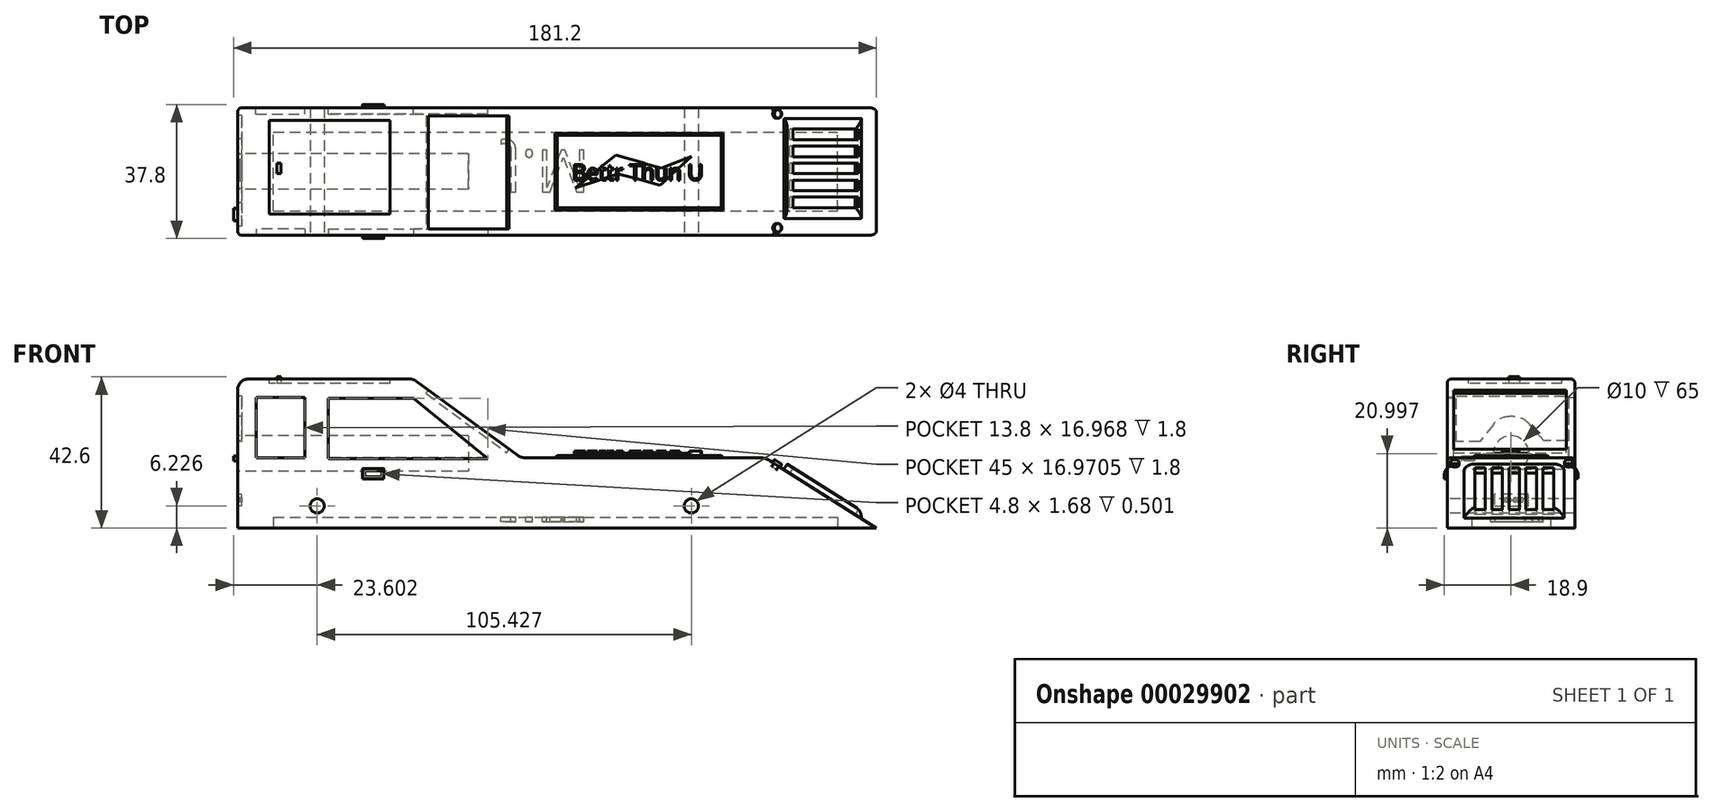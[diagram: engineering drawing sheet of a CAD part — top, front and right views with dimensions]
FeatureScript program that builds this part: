
annotation { "Feature Type Name" : "Feature", "Feature Type Description" : "" }
export const myFeature = defineFeature(function(context is Context, id is Id, definition is map)
    precondition{}
    {
        {
            var Q0;
            Q0=qCreatedBy(makeId("Front.planeOp"),FACE);
            var sketch = newSketch(context, id + "F0", { "sketchPlane" : qUnion([Q0])});
            skLineSegment(sketch, "E0.bottom", {"start": v(-82.47, -33.07) * mm, "end": v(217.53, -33.07) * mm});
            skLineSegment(sketch, "E0.left", {"start": v(-82.47, -33.07) * mm, "end": v(-82.47, 36.93) * mm});
            skLineSegment(sketch, "E1", {"start": v(217.53, -33.07) * mm, "end": v(165.18, 0) * mm});
            skLineSegment(sketch, "E2", {"start": v(165.18, 0) * mm, "end": v(50.43, 0) * mm});
            skLineSegment(sketch, "E3", {"start": v(50.43, 0) * mm, "end": v(0, 36.93) * mm});
            skLineSegment(sketch, "E4", {"start": v(0, 36.93) * mm, "end": v(-82.47, 36.93) * mm});
            skSolve(sketch);
        }
        {
            var Q0;
            Q0=makeQuery(id+"F0.imprint","IMPRINT",FACE,{"disambiguationData":[TD([[makeQuery(id+"F0.imprint","IMPRINT",EDGE,{"derivedFrom":sQuery(id+"F0.wireOp",EDGE,"E0.bottom")}),1.0]])]});
            extrude(context, id + "F1", {"entities" : qUnion([Q0]), "depth" : 60 * mm});
        }
        {
            var Q0;
            Q0=makeQuery(id+"F1.opExtrude","SWEPT_FACE",FACE,{"disambiguationData":[OSD([sQuery(id+"F0.wireOp",EDGE,"E0.left")])]});
            var sketch = newSketch(context, id + "F2", { "sketchPlane" : qUnion([Q0])});
            skCircle(sketch, "E5", {"center": v(30, 1.93) * mm, "radius": 5 * mm});
            skSolve(sketch);
        }
        {
            var Q0;
            Q0=makeQuery(id+"F2.imprint","IMPRINT",FACE,{"disambiguationData":[TD([[makeQuery(id+"F2.imprint","IMPRINT",EDGE,{"derivedFrom":sQuery(id+"F2.wireOp",EDGE,"E5")}),1.0]])]});
            extrude(context, id + "F3", {"entities" : qUnion([Q0]), "operationType" : NewBodyOperationType.REMOVE, "oppositeDirection" : true, "depth" : 65 * mm});
        }
        {
            var Q0;
            Q0=makeQuery(id+"F1.opExtrude","SWEPT_EDGE",EDGE,{"disambiguationData":[OSD([sQuery(id+"F0.wireOp",EDGE,"E1"),sQuery(id+"F0.wireOp",EDGE,"E2")])]});
            fillet(context, id + "F4", {"entities" : qUnion([Q0]), "radius" : 10 * mm, "tangentPropagation" : true, "allowEdgeOverflow" : false});
        }
        {
            var Q0;
            Q0=makeQuery(id+"F1.opExtrude","SWEPT_EDGE",EDGE,{"disambiguationData":[OSD([sQuery(id+"F0.wireOp",EDGE,"E2"),sQuery(id+"F0.wireOp",EDGE,"E3")])]});
            var Q1;
            Q1=makeQuery(id+"F1.opExtrude","SWEPT_EDGE",EDGE,{"disambiguationData":[OSD([sQuery(id+"F0.wireOp",EDGE,"E3"),sQuery(id+"F0.wireOp",EDGE,"E4")])]});
            fillet(context, id + "F5", {"entities" : qUnion([Q0, Q1]), "radius" : 5 * mm, "tangentPropagation" : true, "allowEdgeOverflow" : false});
        }
        {
            var Q0;
            Q0=makeQuery(id+"F1.opExtrude","CAP_FACE",FACE,{"disambiguationData":[OSD([sQuery(id+"F0.wireOp",EDGE,"E0.bottom"),sQuery(id+"F0.wireOp",EDGE,"E0.left"),sQuery(id+"F0.wireOp",EDGE,"E1"),sQuery(id+"F0.wireOp",EDGE,"E2"),sQuery(id+"F0.wireOp",EDGE,"E3"),sQuery(id+"F0.wireOp",EDGE,"E4")])],"isStart":false});
            var sketch = newSketch(context, id + "F6", { "sketchPlane" : qUnion([Q0])});
            skLineSegment(sketch, "E6", {"start": v(0, 27.87) * mm, "end": v(0, 27.87) * mm});
            skLineSegment(sketch, "E7", {"start": v(-40, -0.41) * mm, "end": v(-40, 27.87) * mm});
            skLineSegment(sketch, "E8", {"start": v(-40, 27.87) * mm, "end": v(0, 27.87) * mm});
            skLineSegment(sketch, "E9", {"start": v(-40, -0.41) * mm, "end": v(35, -0.41) * mm});
            skLineSegment(sketch, "E10", {"start": v(35, -0.41) * mm, "end": v(0, 27.87) * mm});
            skLineSegment(sketch, "E11", {"start": v(-73.89, 28.28) * mm, "end": v(-73.89, 0) * mm});
            skLineSegment(sketch, "E12", {"start": v(-50.89, 0) * mm, "end": v(-50.89, 28.28) * mm});
            skLineSegment(sketch, "E13", {"start": v(-50.89, 28.28) * mm, "end": v(-73.89, 28.28) * mm});
            skLineSegment(sketch, "E14", {"start": v(-73.89, 0) * mm, "end": v(-50.89, 0) * mm});
            skSolve(sketch);
        }
        {
            var Q0;
            Q0=qSketchRegion(id+"F6",true);
            extrude(context, id + "F7", {"entities" : qUnion([Q0]), "operationType" : NewBodyOperationType.REMOVE, "oppositeDirection" : true, "depth" : 3 * mm});
        }
        {
            var Q0;
            Q0=makeQuery(id+"F1.opExtrude","CAP_FACE",FACE,{"disambiguationData":[OSD([sQuery(id+"F0.wireOp",EDGE,"E0.bottom"),sQuery(id+"F0.wireOp",EDGE,"E0.left"),sQuery(id+"F0.wireOp",EDGE,"E1"),sQuery(id+"F0.wireOp",EDGE,"E2"),sQuery(id+"F0.wireOp",EDGE,"E3"),sQuery(id+"F0.wireOp",EDGE,"E4")])],"isStart":true});
            var sketch = newSketch(context, id + "F8", { "sketchPlane" : qUnion([Q0])});
            skLineSegment(sketch, "E15", {"start": v(0, 28.28) * mm, "end": v(-35, 0) * mm});
            skLineSegment(sketch, "E16", {"start": v(-35, 0) * mm, "end": v(40, 0) * mm});
            skLineSegment(sketch, "E17", {"start": v(40, 0) * mm, "end": v(40, 28.28) * mm});
            skLineSegment(sketch, "E18", {"start": v(40, 28.28) * mm, "end": v(0, 28.28) * mm});
            skLineSegment(sketch, "E19", {"start": v(51, 28.28) * mm, "end": v(51, 0) * mm});
            skLineSegment(sketch, "E20", {"start": v(51, 0) * mm, "end": v(74, 0) * mm});
            skLineSegment(sketch, "E21", {"start": v(74, 0) * mm, "end": v(74, 28.28) * mm});
            skLineSegment(sketch, "E22", {"start": v(74, 28.28) * mm, "end": v(51, 28.28) * mm});
            skSolve(sketch);
        }
        {
            var Q0;
            Q0=qSketchRegion(id+"F8",true);
            extrude(context, id + "F9", {"entities" : qUnion([Q0]), "operationType" : NewBodyOperationType.REMOVE, "oppositeDirection" : true, "depth" : 3 * mm});
        }
        {
            var Q0;
            Q0=makeQuery(id+"F1.opExtrude","SWEPT_FACE",FACE,{"disambiguationData":[OSD([sQuery(id+"F0.wireOp",EDGE,"E3")])]});
            var sketch = newSketch(context, id + "F10", { "sketchPlane" : qUnion([Q0])});
            skLineSegment(sketch, "E23", {"start": v(-13, -56.94) * mm, "end": v(34, -56.94) * mm});
            skLineSegment(sketch, "E24", {"start": v(34, -56.94) * mm, "end": v(34, -3.94) * mm});
            skLineSegment(sketch, "E25", {"start": v(34, -3.94) * mm, "end": v(-13, -3.94) * mm});
            skLineSegment(sketch, "E26", {"start": v(-13, -3.94) * mm, "end": v(-13, -56.94) * mm});
            skSolve(sketch);
        }
        {
            var Q0;
            Q0=qSketchRegion(id+"F10",true);
            extrude(context, id + "F11", {"entities" : qUnion([Q0]), "operationType" : NewBodyOperationType.REMOVE, "oppositeDirection" : true, "depth" : 2 * mm});
        }
        {
            var Q0;
            Q0=makeQuery(id+"F1.opExtrude","SWEPT_EDGE",EDGE,{"disambiguationData":[OSD([sQuery(id+"F0.wireOp",EDGE,"E0.left"),sQuery(id+"F0.wireOp",EDGE,"E4")])]});
            fillet(context, id + "F12", {"entities" : qUnion([Q0]), "radius" : 5 * mm, "tangentPropagation" : true, "allowEdgeOverflow" : false});
        }
        {
            var Q0;
            Q0=makeQuery(id+"F1.opExtrude","CAP_FACE",FACE,{"disambiguationData":[OSD([sQuery(id+"F0.wireOp",EDGE,"E0.bottom"),sQuery(id+"F0.wireOp",EDGE,"E0.left"),sQuery(id+"F0.wireOp",EDGE,"E1"),sQuery(id+"F0.wireOp",EDGE,"E2"),sQuery(id+"F0.wireOp",EDGE,"E3"),sQuery(id+"F0.wireOp",EDGE,"E4")])],"isStart":false});
            var sketch = newSketch(context, id + "F13", { "sketchPlane" : qUnion([Q0])});
            skLineSegment(sketch, "E27", {"start": v(-23.82, -5.07) * mm, "end": v(-13.82, -5.07) * mm});
            skLineSegment(sketch, "E28", {"start": v(-13.82, -5.07) * mm, "end": v(-13.82, -10.07) * mm});
            skLineSegment(sketch, "E29", {"start": v(-13.82, -10.07) * mm, "end": v(-23.82, -10.07) * mm});
            skLineSegment(sketch, "E30", {"start": v(-23.82, -10.07) * mm, "end": v(-23.82, -5.07) * mm});
            skLineSegment(sketch, "E31", {"start": v(-22.8, -6.15) * mm, "end": v(-22.8, -8.95) * mm});
            skLineSegment(sketch, "E32", {"start": v(-22.8, -8.95) * mm, "end": v(-14.8, -8.95) * mm});
            skLineSegment(sketch, "E33", {"start": v(-14.8, -8.95) * mm, "end": v(-14.8, -6.15) * mm});
            skLineSegment(sketch, "E34", {"start": v(-14.8, -6.15) * mm, "end": v(-22.8, -6.15) * mm});
            skSolve(sketch);
        }
        {
            var Q0;
            Q0=qSketchRegion(id+"F13",true);
            extrude(context, id + "F14", {"entities" : qUnion([Q0]), "operationType" : NewBodyOperationType.ADD, "depth" : 1.5 * mm});
        }
        {
            var Q0;
            Q0=makeQuery(id+"F1.opExtrude","CAP_FACE",FACE,{"disambiguationData":[OSD([sQuery(id+"F0.wireOp",EDGE,"E0.bottom"),sQuery(id+"F0.wireOp",EDGE,"E0.left"),sQuery(id+"F0.wireOp",EDGE,"E1"),sQuery(id+"F0.wireOp",EDGE,"E2"),sQuery(id+"F0.wireOp",EDGE,"E3"),sQuery(id+"F0.wireOp",EDGE,"E4")])],"isStart":true});
            var sketch = newSketch(context, id + "F15", { "sketchPlane" : qUnion([Q0])});
            skLineSegment(sketch, "E35", {"start": v(13.79, -4.77) * mm, "end": v(13.79, -9.77) * mm});
            skLineSegment(sketch, "E36", {"start": v(13.79, -9.77) * mm, "end": v(23.79, -9.77) * mm});
            skLineSegment(sketch, "E37", {"start": v(23.79, -9.77) * mm, "end": v(23.79, -4.77) * mm});
            skLineSegment(sketch, "E38", {"start": v(23.79, -4.77) * mm, "end": v(13.79, -4.77) * mm});
            skLineSegment(sketch, "E39", {"start": v(14.77, -5.87) * mm, "end": v(14.77, -8.67) * mm});
            skLineSegment(sketch, "E40", {"start": v(14.77, -8.67) * mm, "end": v(22.77, -8.67) * mm});
            skLineSegment(sketch, "E41", {"start": v(22.77, -8.67) * mm, "end": v(22.77, -5.87) * mm});
            skLineSegment(sketch, "E42", {"start": v(22.77, -5.87) * mm, "end": v(14.77, -5.87) * mm});
            skSolve(sketch);
        }
        {
            var Q0;
            Q0=qSketchRegion(id+"F15",true);
            extrude(context, id + "F16", {"entities" : qUnion([Q0]), "operationType" : NewBodyOperationType.ADD, "depth" : 1.5 * mm});
        }
        {
            var Q0;
            Q0=makeQuery(id+"F16.opExtrude","CAP_EDGE",EDGE,{"disambiguationData":[OSD([sQuery(id+"F15.wireOp",EDGE,"E38")])],"isStart":false});
            fillet(context, id + "F17", {"entities" : qUnion([Q0]), "radius" : 5 * mm, "tangentPropagation" : true, "allowEdgeOverflow" : false});
        }
        {
            var Q0;
            Q0=makeQuery(id+"F14.opExtrude","CAP_EDGE",EDGE,{"disambiguationData":[OSD([sQuery(id+"F13.wireOp",EDGE,"E27")])],"isStart":false});
            fillet(context, id + "F18", {"entities" : qUnion([Q0]), "radius" : 5 * mm, "tangentPropagation" : true, "allowEdgeOverflow" : false});
        }
        {
            var Q0;
            Q0=makeQuery(id+"F1.opExtrude","SWEPT_FACE",FACE,{"disambiguationData":[OSD([sQuery(id+"F0.wireOp",EDGE,"E0.left")])]});
            var sketch = newSketch(context, id + "F19", { "sketchPlane" : qUnion([Q0])});
            skLineSegment(sketch, "E43", {"start": v(3.67, 28.92) * mm, "end": v(3.67, 7.92) * mm});
            skLineSegment(sketch, "E44", {"start": v(3.67, 7.92) * mm, "end": v(14.67, 7.92) * mm});
            skLineSegment(sketch, "E45", {"start": v(14.67, 7.92) * mm, "end": v(21.44, 15.81) * mm});
            skLineSegment(sketch, "E46", {"start": v(29.03, 19.3) * mm, "end": v(30.56, 19.3) * mm});
            skLineSegment(sketch, "E47", {"start": v(38.43, 15.46) * mm, "end": v(44.67, 7.49) * mm});
            skLineSegment(sketch, "E48", {"start": v(44.67, 7.49) * mm, "end": v(55.67, 7.49) * mm});
            skLineSegment(sketch, "E49", {"start": v(55.67, 7.49) * mm, "end": v(55.67, 28.92) * mm});
            skLineSegment(sketch, "E50", {"start": v(55.67, 28.92) * mm, "end": v(3.67, 28.92) * mm});
            skPoint(sketch, "E51.visualSharp", {"position": v(24.43, 19.3) * mm});
            skArc(sketch, "E51.filletArc", {"start": v(29.03, 19.3) * mm, "mid": v(24.85, 18.4) * mm, "end": v(21.44, 15.81) * mm});
            skPoint(sketch, "E52.visualSharp", {"position": v(35.43, 19.3) * mm});
            skArc(sketch, "E52.filletArc", {"start": v(38.43, 15.46) * mm, "mid": v(34.94, 18.3) * mm, "end": v(30.56, 19.3) * mm});
            skLineSegment(sketch, "E53", {"start": v(16.08, 9.56) * mm, "end": v(15.58, 8.97) * mm});
            skLineSegment(sketch, "E54", {"start": v(21.84, -17.18) * mm, "end": v(37.84, -17.18) * mm});
            skLineSegment(sketch, "E55", {"start": v(37.84, -17.18) * mm, "end": v(37.84, -22.68) * mm});
            skLineSegment(sketch, "E56", {"start": v(37.84, -22.68) * mm, "end": v(21.84, -22.68) * mm});
            skLineSegment(sketch, "E57", {"start": v(21.84, -22.68) * mm, "end": v(21.84, -17.18) * mm});
            skText(sketch, "E58", { "text": "062-002", "fontName": "OpenSans-Regular.ttf"});
            const initialGuessF19  = {"E58": [0.0242, -0.02085, 1, 0, 0.002]};
            skSetInitialGuess(sketch, initialGuessF19);
            skSolve(sketch);
        }
        {
            var Q0;
            Q0=makeQuery(id+"F1.opExtrude","SWEPT_FACE",FACE,{"disambiguationData":[OSD([sQuery(id+"F0.wireOp",EDGE,"E1")])]});
            var sketch = newSketch(context, id + "F20", { "sketchPlane" : qUnion([Q0])});
            skLineSegment(sketch, "E59", {"start": v(150.04, -5.03) * mm, "end": v(150.04, -52.03) * mm});
            skLineSegment(sketch, "E60", {"start": v(150.04, -52.03) * mm, "end": v(193.04, -52.03) * mm});
            skLineSegment(sketch, "E61", {"start": v(193.04, -52.03) * mm, "end": v(193.04, -5.03) * mm});
            skLineSegment(sketch, "E62", {"start": v(193.04, -5.03) * mm, "end": v(150.04, -5.03) * mm});
            skLineSegment(sketch, "E63", {"start": v(153.34, -10.03) * mm, "end": v(189.74, -10.03) * mm});
            skLineSegment(sketch, "E64", {"start": v(189.74, -10.03) * mm, "end": v(189.74, -15.03) * mm});
            skLineSegment(sketch, "E65", {"start": v(189.74, -15.03) * mm, "end": v(153.34, -15.03) * mm});
            skLineSegment(sketch, "E66", {"start": v(153.34, -15.03) * mm, "end": v(153.34, -10.03) * mm});
            skLineSegment(sketch, "E67", {"start": v(153.34, -18.03) * mm, "end": v(189.74, -18.03) * mm});
            skLineSegment(sketch, "E68", {"start": v(189.74, -18.03) * mm, "end": v(189.74, -23.03) * mm});
            skLineSegment(sketch, "E69", {"start": v(189.74, -23.03) * mm, "end": v(153.34, -23.03) * mm});
            skLineSegment(sketch, "E70", {"start": v(153.34, -23.03) * mm, "end": v(153.34, -18.03) * mm});
            skLineSegment(sketch, "E71", {"start": v(153.34, -26.03) * mm, "end": v(189.74, -26.03) * mm});
            skLineSegment(sketch, "E72", {"start": v(189.74, -26.03) * mm, "end": v(189.74, -31.03) * mm});
            skLineSegment(sketch, "E73", {"start": v(189.74, -31.03) * mm, "end": v(153.34, -31.03) * mm});
            skLineSegment(sketch, "E74", {"start": v(153.34, -31.03) * mm, "end": v(153.34, -26.03) * mm});
            skLineSegment(sketch, "E75", {"start": v(153.34, -34.03) * mm, "end": v(189.74, -34.03) * mm});
            skLineSegment(sketch, "E76", {"start": v(189.74, -34.03) * mm, "end": v(189.74, -39.03) * mm});
            skLineSegment(sketch, "E77", {"start": v(189.74, -39.03) * mm, "end": v(153.34, -39.03) * mm});
            skLineSegment(sketch, "E78", {"start": v(153.34, -39.03) * mm, "end": v(153.34, -34.03) * mm});
            skLineSegment(sketch, "E79", {"start": v(153.34, -42.03) * mm, "end": v(189.74, -42.03) * mm});
            skLineSegment(sketch, "E80", {"start": v(189.74, -42.03) * mm, "end": v(189.74, -47.03) * mm});
            skLineSegment(sketch, "E81", {"start": v(189.74, -47.03) * mm, "end": v(153.34, -47.03) * mm});
            skLineSegment(sketch, "E82", {"start": v(153.34, -47.03) * mm, "end": v(153.34, -42.03) * mm});
            skSolve(sketch);
        }
        {
            var Q0;
            Q0=qSketchRegion(id+"F20",true);
            extrude(context, id + "F21", {"entities" : qUnion([Q0]), "operationType" : NewBodyOperationType.ADD, "depth" : 3 * mm});
        }
        {
            var Q0;
            Q0=makeQuery(id+"F21.opExtrude","CAP_EDGE",EDGE,{"disambiguationData":[OSD([sQuery(id+"F20.wireOp",EDGE,"E61")])],"isStart":false});
            var Q1;
            Q1=makeQuery(id+"F21.opExtrude","CAP_EDGE",EDGE,{"disambiguationData":[OSD([sQuery(id+"F20.wireOp",EDGE,"E60")])],"isStart":false});
            var Q2;
            Q2=makeQuery(id+"F21.opExtrude","CAP_EDGE",EDGE,{"disambiguationData":[OSD([sQuery(id+"F20.wireOp",EDGE,"E62")])],"isStart":false});
            fillet(context, id + "F22", {"entities" : qUnion([Q0, Q1, Q2]), "radius" : 5 * mm, "tangentPropagation" : true, "allowEdgeOverflow" : false});
        }
        {
            var Q0;
            Q0=makeQuery(id+"F1.opExtrude","SWEPT_FACE",FACE,{"disambiguationData":[OSD([sQuery(id+"F0.wireOp",EDGE,"E2")])]});
            var sketch = newSketch(context, id + "F23", { "sketchPlane" : qUnion([Q0])});
            skLineSegment(sketch, "E83", {"start": v(62.58, -8) * mm, "end": v(62.58, -52) * mm});
            skLineSegment(sketch, "E84", {"start": v(62.58, -52) * mm, "end": v(149.58, -52) * mm});
            skLineSegment(sketch, "E85", {"start": v(149.58, -52) * mm, "end": v(149.58, -8) * mm});
            skLineSegment(sketch, "E86", {"start": v(149.58, -8) * mm, "end": v(62.58, -8) * mm});
            skSolve(sketch);
        }
        {
            var Q0;
            Q0=qSketchRegion(id+"F23",true);
            extrude(context, id + "F24", {"entities" : qUnion([Q0]), "operationType" : NewBodyOperationType.ADD, "depth" : 1 * mm});
        }
        {
            var Q0;
            Q0=makeQuery(id+"F24.opExtrude","CAP_EDGE",EDGE,{"disambiguationData":[OSD([sQuery(id+"F23.wireOp",EDGE,"E84")])],"isStart":false});
            var Q1;
            Q1=makeQuery(id+"F24.opExtrude","CAP_EDGE",EDGE,{"disambiguationData":[OSD([sQuery(id+"F23.wireOp",EDGE,"E85")])],"isStart":false});
            var Q2;
            Q2=makeQuery(id+"F24.opExtrude","CAP_EDGE",EDGE,{"disambiguationData":[OSD([sQuery(id+"F23.wireOp",EDGE,"E86")])],"isStart":false});
            var Q3;
            Q3=makeQuery(id+"F24.opExtrude","CAP_EDGE",EDGE,{"disambiguationData":[OSD([sQuery(id+"F23.wireOp",EDGE,"E83")])],"isStart":false});
            chamfer(context, id + "F25", {"entities" : qUnion([Q0, Q1, Q2, Q3]), "width" : 5 * mm, "tangentPropagation" : true});
        }
        {
            var Q0;
            Q0=qSketchRegion(id+"F19",true);
            extrude(context, id + "F26", {"entities" : qUnion([Q0]), "operationType" : NewBodyOperationType.REMOVE, "oppositeDirection" : true, "depth" : 2 * mm});
        }
        {
            var Q0;
            Q0=makeQuery(id+"F1.opExtrude","SWEPT_FACE",FACE,{"disambiguationData":[OSD([sQuery(id+"F0.wireOp",EDGE,"E4")])]});
            var sketch = newSketch(context, id + "F27", { "sketchPlane" : qUnion([Q0])});
            skLineSegment(sketch, "E87", {"start": v(-67.65, -6.07) * mm, "end": v(-67.65, -49.96) * mm});
            skLineSegment(sketch, "E88", {"start": v(-67.65, -49.96) * mm, "end": v(-11.01, -49.96) * mm});
            skLineSegment(sketch, "E89", {"start": v(-11.01, -49.96) * mm, "end": v(-11.01, -6.07) * mm});
            skLineSegment(sketch, "E90", {"start": v(-11.01, -6.07) * mm, "end": v(-67.65, -6.07) * mm});
            skSolve(sketch);
        }
        {
            var Q0;
            Q0=makeQuery(id+"F27.imprint","IMPRINT",FACE,{"disambiguationData":[TD([[makeQuery(id+"F27.imprint","IMPRINT",EDGE,{"derivedFrom":sQuery(id+"F27.wireOp",EDGE,"E87")}),1.0]])]});
            extrude(context, id + "F28", {"entities" : qUnion([Q0]), "operationType" : NewBodyOperationType.REMOVE, "oppositeDirection" : true, "depth" : 2 * mm});
        }
        {
            var Q0;
            Q0=makeQuery(id+"F1.opExtrude","SWEPT_FACE",FACE,{"disambiguationData":[OSD([sQuery(id+"F0.wireOp",EDGE,"E0.left")])]});
            var sketch = newSketch(context, id + "F29", { "sketchPlane" : qUnion([Q0])});
            skLineSegment(sketch, "E91", {"start": v(47.24, 0.76) * mm, "end": v(47.24, -1.54) * mm});
            skLineSegment(sketch, "E92", {"start": v(47.24, -1.54) * mm, "end": v(53.14, -1.54) * mm});
            skLineSegment(sketch, "E93", {"start": v(53.14, -1.54) * mm, "end": v(53.14, 0.76) * mm});
            skLineSegment(sketch, "E94", {"start": v(53.14, 0.76) * mm, "end": v(47.24, 0.76) * mm});
            skLineSegment(sketch, "E95", {"start": v(47.87, 0) * mm, "end": v(47.87, -1.04) * mm});
            skLineSegment(sketch, "E96", {"start": v(47.87, -1.04) * mm, "end": v(52.6, -1.04) * mm});
            skLineSegment(sketch, "E97", {"start": v(52.6, -1.04) * mm, "end": v(52.6, 0) * mm});
            skLineSegment(sketch, "E98", {"start": v(52.6, 0) * mm, "end": v(47.87, 0) * mm});
            skSolve(sketch);
        }
        {
            var Q0;
            Q0=qSketchRegion(id+"F29",true);
            extrude(context, id + "F30", {"entities" : qUnion([Q0]), "operationType" : NewBodyOperationType.ADD, "depth" : 2 * mm});
        }
        {
            var Q0;
            Q0=makeQuery(id+"F28.boolean.opBoolean","COPY",FACE,{"derivedFrom":makeQuery(id+"F28.opExtrude","CAP_FACE",FACE,{"disambiguationData":[OSD([sQuery(id+"F27.wireOp",EDGE,"E87"),sQuery(id+"F27.wireOp",EDGE,"E88"),sQuery(id+"F27.wireOp",EDGE,"E89"),sQuery(id+"F27.wireOp",EDGE,"E90")])],"isStart":false})});
            var sketch = newSketch(context, id + "F31", { "sketchPlane" : qUnion([Q0])});
            skLineSegment(sketch, "E99", {"start": v(-64.12, -26.05) * mm, "end": v(-64.12, -31.05) * mm});
            skLineSegment(sketch, "E100", {"start": v(-64.12, -31.05) * mm, "end": v(-62.12, -31.05) * mm});
            skLineSegment(sketch, "E101", {"start": v(-62.12, -31.05) * mm, "end": v(-62.12, -26.05) * mm});
            skLineSegment(sketch, "E102", {"start": v(-62.12, -26.05) * mm, "end": v(-64.12, -26.05) * mm});
            skSolve(sketch);
        }
        {
            var Q0;
            Q0=qSketchRegion(id+"F31",true);
            extrude(context, id + "F32", {"entities" : qUnion([Q0]), "operationType" : NewBodyOperationType.ADD, "depth" : 3 * mm});
        }
        {
            var Q0;
            {var subQ0=sQuery(id+"F0.wireOp",EDGE,"E1");var subQ1=sQuery(id+"F0.wireOp",EDGE,"E0.bottom");Q0=makeQuery(id+"F21.boolean.opBoolean","SPLIT",FACE,{"disambiguationData":[TD([makeQuery(id+"F1.opExtrude","SWEPT_FACE",FACE,{"disambiguationData":[OSD([subQ1])]})])],"derivedFrom":makeQuery(id+"F1.opExtrude","SWEPT_FACE",FACE,{"disambiguationData":[OSD([subQ0])]})});}
            var sketch = newSketch(context, id + "F33", { "sketchPlane" : qUnion([Q0])});
            skCircle(sketch, "E103", {"center": v(145.91, -56.44) * mm, "radius": 2 * mm});
            skCircle(sketch, "E104", {"center": v(145.91, -2.94) * mm, "radius": 2 * mm});
            skSolve(sketch);
        }
        {
            var Q0;
            Q0=qSketchRegion(id+"F33",true);
            extrude(context, id + "F34", {"entities" : qUnion([Q0]), "operationType" : NewBodyOperationType.ADD, "depth" : 1.6 * mm});
        }
        {
            var Q0;
            Q0=makeQuery(id+"F1.opExtrude","SWEPT_FACE",FACE,{"disambiguationData":[OSD([sQuery(id+"F0.wireOp",EDGE,"E0.bottom")])]});
            var sketch = newSketch(context, id + "F35", { "sketchPlane" : qUnion([Q0])});
            skLineSegment(sketch, "E105.bottom", {"start": v(-65.68, 48.5) * mm, "end": v(199.32, 48.5) * mm});
            skLineSegment(sketch, "E105.top", {"start": v(-65.68, 11.5) * mm, "end": v(199.32, 11.5) * mm});
            skLineSegment(sketch, "E105.right", {"start": v(199.32, 48.5) * mm, "end": v(199.32, 11.5) * mm});
            skLineSegment(sketch, "E106", {"start": v(-65.68, 48.5) * mm, "end": v(-65.68, 11.5) * mm});
            skSolve(sketch);
        }
        {
            var Q0;
            Q0=qSketchRegion(id+"F35",true);
            extrude(context, id + "F36", {"entities" : qUnion([Q0]), "operationType" : NewBodyOperationType.REMOVE, "oppositeDirection" : true, "depth" : 5 * mm});
        }
        {
            var Q0;
            Q0=makeQuery(id+"F1.opExtrude","CAP_EDGE",EDGE,{"disambiguationData":[OSD([sQuery(id+"F0.wireOp",EDGE,"E2")])],"isStart":false});
            var Q1;
            Q1=makeQuery(id+"F1.opExtrude","CAP_EDGE",EDGE,{"disambiguationData":[OSD([sQuery(id+"F0.wireOp",EDGE,"E3")])],"isStart":false});
            var Q2;
            Q2=makeQuery(id+"F1.opExtrude","CAP_EDGE",EDGE,{"disambiguationData":[OSD([sQuery(id+"F0.wireOp",EDGE,"E4")])],"isStart":false});
            var Q3;
            Q3=makeQuery(id+"F1.opExtrude","CAP_EDGE",EDGE,{"disambiguationData":[OSD([sQuery(id+"F0.wireOp",EDGE,"E2")])],"isStart":true});
            fillet(context, id + "F37", {"entities" : qUnion([Q0, Q1, Q2, Q3]), "radius" : 2 * mm, "tangentPropagation" : true, "allowEdgeOverflow" : false});
        }
        {
            var Q0;
            Q0=makeQuery(id+"F24.opExtrude","CAP_FACE",FACE,{"disambiguationData":[OSD([sQuery(id+"F23.wireOp",EDGE,"E83"),sQuery(id+"F23.wireOp",EDGE,"E84"),sQuery(id+"F23.wireOp",EDGE,"E85"),sQuery(id+"F23.wireOp",EDGE,"E86")])],"isStart":false});
            var sketch = newSketch(context, id + "F38", { "sketchPlane" : qUnion([Q0])});
            skText(sketch, "E107", { "text": "Bettr Thun U", "fontName": "OpenSans-Regular.ttf"});
            const initialGuessF38  = {"E107": [0.07456, -0.03404, 1, 0, 0.00745]};
            skSetInitialGuess(sketch, initialGuessF38);
            skSolve(sketch);
        }
        {
            var Q0;
            Q0=qSketchRegion(id+"F38",true);
            extrude(context, id + "F39", {"entities" : qUnion([Q0]), "operationType" : NewBodyOperationType.ADD, "depth" : 2 * mm});
        }
        {
            var Q0;
            {var subQ0=sQuery(id+"F23.wireOp",EDGE,"E83");var subQ1=sQuery(id+"F23.wireOp",EDGE,"E84");var subQ2=sQuery(id+"F23.wireOp",EDGE,"E85");var subQ3=sQuery(id+"F23.wireOp",EDGE,"E86");Q0=makeQuery(id+"F39.boolean.opBoolean","SPLIT",FACE,{"disambiguationData":[TD([makeQuery(id+"F25.opChamfer","BLEND_FACE",FACE,{"disambiguationData":[OSD([subQ0])]})])],"derivedFrom":makeQuery(id+"F24.opExtrude","CAP_FACE",FACE,{"disambiguationData":[OSD([subQ0,subQ1,subQ2,subQ3])],"isStart":false})});}
            var sketch = newSketch(context, id + "F40", { "sketchPlane" : qUnion([Q0])});
            skLineSegment(sketch, "E108", {"start": v(76.12, -37.77) * mm, "end": v(95.2, -22.21) * mm});
            skLineSegment(sketch, "E109", {"start": v(95.2, -22.21) * mm, "end": v(116.5, -28.5) * mm});
            skLineSegment(sketch, "E110", {"start": v(116.5, -28.5) * mm, "end": v(130.59, -22.95) * mm});
            skLineSegment(sketch, "E111", {"start": v(130.59, -22.95) * mm, "end": v(115.9, -36.45) * mm});
            skLineSegment(sketch, "E112", {"start": v(115.9, -36.45) * mm, "end": v(96.11, -31.07) * mm});
            skLineSegment(sketch, "E113", {"start": v(96.11, -31.07) * mm, "end": v(76.12, -37.77) * mm});
            skSolve(sketch);
        }
        {
            var Q0;
            Q0=qSketchRegion(id+"F40",true);
            extrude(context, id + "F41", {"entities" : qUnion([Q0]), "operationType" : NewBodyOperationType.ADD, "depth" : 1 * mm});
        }
        {
            var Q0;
            Q0=makeQuery(id+"F36.boolean.opBoolean","COPY",FACE,{"derivedFrom":makeQuery(id+"F36.opExtrude","CAP_FACE",FACE,{"disambiguationData":[OSD([sQuery(id+"F35.wireOp",EDGE,"E105.bottom"),sQuery(id+"F35.wireOp",EDGE,"E105.top"),sQuery(id+"F35.wireOp",EDGE,"E105.right"),sQuery(id+"F35.wireOp",EDGE,"E106")])],"isStart":false})});
            var sketch = newSketch(context, id + "F42", { "sketchPlane" : qUnion([Q0])});
            skText(sketch, "E114", { "text": "J.M", "fontName": "OpenSans-Regular.ttf"});
            const initialGuessF42  = {"E114": [0.04333, 0.02004, 1, 0, 0.01982]};
            skSetInitialGuess(sketch, initialGuessF42);
            skSolve(sketch);
        }
        {
            var Q0;
            Q0=qSketchRegion(id+"F42",true);
            extrude(context, id + "F43", {"entities" : qUnion([Q0]), "operationType" : NewBodyOperationType.ADD, "depth" : 2 * mm});
        }
        {
            var Q0;
            Q0=makeQuery(id+"F1.opExtrude","SWEPT_BODY",BODY,{"disambiguationData":[OSD([sQuery(id+"F0.wireOp",EDGE,"E0.bottom"),sQuery(id+"F0.wireOp",EDGE,"E0.left"),sQuery(id+"F0.wireOp",EDGE,"E1"),sQuery(id+"F0.wireOp",EDGE,"E2"),sQuery(id+"F0.wireOp",EDGE,"E3"),sQuery(id+"F0.wireOp",EDGE,"E4")])]});
            var Q1;
            {var subQ0=sQuery(id+"F0.wireOp",EDGE,"E2");var subQ1=sQuery(id+"F0.wireOp",EDGE,"E3");Q1=makeQuery(id+"F37.opFillet","BLEND_VERTEX",VERTEX,{"blendedFrom":[makeQuery(id+"F5.opFillet","BLEND_EDGE",EDGE,{"blendedFrom":[makeQuery(id+"F1.opExtrude","SWEPT_EDGE",EDGE,{"disambiguationData":[OSD([subQ0,subQ1])]}),makeQuery(id+"F1.opExtrude","CAP_FACE",FACE,{"disambiguationData":[OSD([sQuery(id+"F0.wireOp",EDGE,"E0.bottom"),sQuery(id+"F0.wireOp",EDGE,"E0.left"),sQuery(id+"F0.wireOp",EDGE,"E1"),subQ0,subQ1,sQuery(id+"F0.wireOp",EDGE,"E4")])],"isStart":false})],"blendedInto":[makeQuery(id+"F1.opExtrude","CAP_FACE",FACE,{"disambiguationData":[OSD([sQuery(id+"F0.wireOp",EDGE,"E0.bottom"),sQuery(id+"F0.wireOp",EDGE,"E0.left"),sQuery(id+"F0.wireOp",EDGE,"E1"),subQ0,subQ1,sQuery(id+"F0.wireOp",EDGE,"E4")])],"isStart":false})]}),makeQuery(id+"F1.opExtrude","CAP_EDGE",EDGE,{"disambiguationData":[OSD([subQ0])],"isStart":false}),makeQuery(id+"F5.opFillet","BLEND_FACE",FACE,{"disambiguationData":[OSD([subQ0,subQ1])]}),makeQuery(id+"F1.opExtrude","SWEPT_FACE",FACE,{"disambiguationData":[OSD([subQ0])]})],"blendedInto":[makeQuery(id+"F5.opFillet","BLEND_FACE",FACE,{"disambiguationData":[OSD([subQ0,subQ1])]}),makeQuery(id+"F1.opExtrude","SWEPT_FACE",FACE,{"disambiguationData":[OSD([subQ0])]})]});}
            transform(context, id + "F44", {"entities" : qUnion([Q0]), "transformType" : TransformType.SCALE_UNIFORMLY, "scale" : .6, "makeCopy" : false, "scalePoint" : qUnion([Q1])});
        }
        {
            var Q0;
            {var subQ0=sQuery(id+"F0.wireOp",EDGE,"E0.bottom");var subQ1=sQuery(id+"F0.wireOp",EDGE,"E0.left");var subQ2=sQuery(id+"F0.wireOp",EDGE,"E1");var subQ3=sQuery(id+"F0.wireOp",EDGE,"E2");var subQ4=sQuery(id+"F0.wireOp",EDGE,"E3");var subQ5=sQuery(id+"F0.wireOp",EDGE,"E4");Q0=makeQuery(id+"F14.boolean.opBoolean","SPLIT",FACE,{"disambiguationData":[TD([makeQuery(id+"F1.opExtrude","SWEPT_FACE",FACE,{"disambiguationData":[OSD([subQ0])]})])],"derivedFrom":makeQuery(id+"F1.opExtrude","CAP_FACE",FACE,{"disambiguationData":[OSD([subQ0,subQ1,subQ2,subQ3,subQ4,subQ5])],"isStart":false})});}
            var sketch = newSketch(context, id + "F45", { "sketchPlane" : qUnion([Q0])});
            skCircle(sketch, "E115", {"center": v(-6.26, -13.61) * mm, "radius": 2 * mm});
            skCircle(sketch, "E116", {"center": v(99.17, -13.61) * mm, "radius": 2 * mm});
            skSolve(sketch);
        }
        {
            var Q0;
            Q0=qSketchRegion(id+"F45",true);
            extrude(context, id + "F46", {"entities" : qUnion([Q0]), "operationType" : NewBodyOperationType.REMOVE, "endBound" : BoundingType.THROUGH_ALL, "oppositeDirection" : true, "depth" : 25 * mm});
        }
        {
            var Q0;
            {var subQ0=sQuery(id+"F0.wireOp",EDGE,"E0.left");var subQ17=sQuery(id+"F0.wireOp",EDGE,"E0.bottom");var subQ24=makeQuery(id+"F1.opExtrude","SWEPT_FACE",FACE,{"disambiguationData":[OSD([subQ17])]});Q0=makeQuery(id+"F30.boolean.opBoolean","SPLIT",FACE,{"disambiguationData":[TD([subQ24])],"derivedFrom":makeQuery(id+"F26.boolean.opBoolean","SPLIT",FACE,{"disambiguationData":[TD([subQ24])],"derivedFrom":makeQuery(id+"F1.opExtrude","SWEPT_FACE",FACE,{"disambiguationData":[OSD([subQ0])]})})});}
            var sketch = newSketch(context, id + "F47", { "sketchPlane" : qUnion([Q0])});
            skCircle(sketch, "E117", {"center": v(41.2, 1.16) * mm, "radius": 5 * mm});
            skSolve(sketch);
        }
        {
            var Q0;
            Q0=qSketchRegion(id+"F47",true);
            extrude(context, id + "F48", {"entities" : qUnion([Q0]), "operationType" : NewBodyOperationType.REMOVE, "oppositeDirection" : true, "depth" : 65 * mm});
        }
    });
